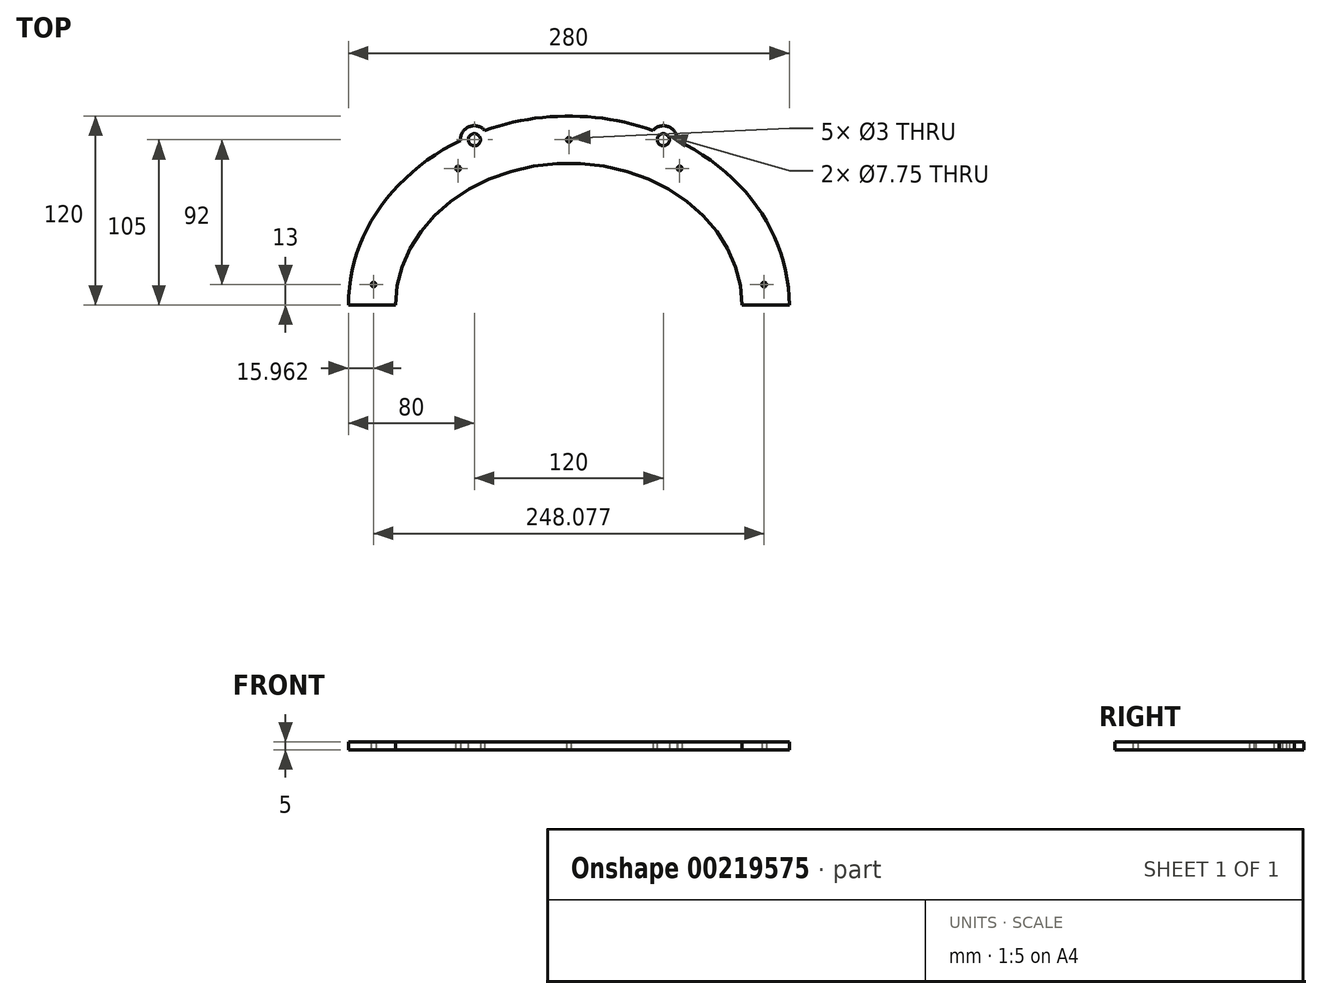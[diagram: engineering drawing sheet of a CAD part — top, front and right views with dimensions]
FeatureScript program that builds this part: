
annotation { "Feature Type Name" : "Feature", "Feature Type Description" : "" }
export const myFeature = defineFeature(function(context is Context, id is Id, definition is map)
    precondition{}
    {
        {
            var Q0;
            Q0=qCreatedBy(makeId("Top.planeOp"),FACE);
            var sketch = newSketch(context, id + "F0", { "sketchPlane" : qUnion([Q0])});
            skEllipse(sketch, "E0", {"center": v(0, 0) * mm, "majorRadius": 140 * mm, "minorRadius": 120 * mm, "majorAxis": v(1, 0)});
            skLineSegment(sketch, "E1", {"start": v(0, 0) * mm, "end": v(0, 120) * mm, "construction": true});
            skLineSegment(sketch, "E2", {"start": v(0, 0) * mm, "end": v(140, 0) * mm, "construction": true});
            skPoint(sketch, "E2.endSnap0", {"position": v(140, 0) * mm});
            skEllipse(sketch, "E3", {"center": v(0, 0) * mm, "majorRadius": 110 * mm, "minorRadius": 90 * mm, "majorAxis": v(1, 0)});
            skLineSegment(sketch, "E4", {"start": v(110, 0) * mm, "end": v(140, 0) * mm, "construction": true});
            skLineSegment(sketch, "E5", {"start": v(0, 90) * mm, "end": v(0, 120) * mm, "construction": true});
            skCircle(sketch, "E6", {"center": v(-60, 105) * mm, "radius": 3.88 * mm});
            skCircle(sketch, "E7", {"center": v(60, 105) * mm, "radius": 3.88 * mm});
            skLineSegment(sketch, "E8", {"start": v(-60, 105) * mm, "end": v(60, 105) * mm, "construction": true});
            skPoint(sketch, "E9", {"position": v(0, 105) * mm});
            skLineSegment(sketch, "E10", {"start": v(-110, 0) * mm, "end": v(-140, 0) * mm});
            skLineSegment(sketch, "E11", {"start": v(110, 0) * mm, "end": v(140, 0) * mm});
            skPoint(sketch, "E12", {"position": v(125, 0) * mm});
            skEllipse(sketch, "E13", {"center": v(0, 0) * mm, "majorRadius": 125 * mm, "minorRadius": 105 * mm, "majorAxis": v(1, 0), "construction": true});
            skLineSegment(sketch, "E14", {"start": v(0, 0) * mm, "end": v(70.33, 86.8) * mm, "construction": true});
            skLineSegment(sketch, "E15", {"start": v(-124.04, 13) * mm, "end": v(0, 0) * mm, "construction": true});
            skLineSegment(sketch, "E16", {"start": v(0, 0) * mm, "end": v(-70.33, 86.8) * mm, "construction": true});
            skLineSegment(sketch, "E17", {"start": v(0, 0) * mm, "end": v(124.04, 13) * mm, "construction": true});
            skCircle(sketch, "E18", {"center": v(-124.04, 13) * mm, "radius": 1.5 * mm});
            skCircle(sketch, "E19", {"center": v(-70.33, 86.8) * mm, "radius": 1.5 * mm});
            skCircle(sketch, "E20", {"center": v(70.33, 86.8) * mm, "radius": 1.5 * mm});
            skCircle(sketch, "E21", {"center": v(124.04, 13) * mm, "radius": 1.5 * mm});
            skCircle(sketch, "E22", {"center": v(0, 105) * mm, "radius": 1.5 * mm});
            skCircle(sketch, "E23", {"center": v(-60, 105) * mm, "radius": 8.88 * mm});
            skCircle(sketch, "E24", {"center": v(60, 105) * mm, "radius": 8.88 * mm});
            skSolve(sketch);
        }
        {
            var Q0;
            Q0=makeQuery(id+"F0.imprint","IMPRINT",FACE,{"disambiguationData":[TD([[makeQuery(id+"F0.imprint","IMPRINT",EDGE,{"derivedFrom":sQuery(id+"F0.wireOp",EDGE,"E6")}),-1.0]])]});
            var Q1;
            {var subQ8=sQuery(id+"F0.wireOp",EDGE,"E10");Q1=makeQuery(id+"F0.imprint","IMPRINT",FACE,{"disambiguationData":[TD([[makeQuery(id+"F0.imprint","IMPRINT",EDGE,{"derivedFrom":subQ8}),-1.0]])]});}
            var Q2;
            Q2=makeQuery(id+"F0.imprint","IMPRINT",FACE,{"disambiguationData":[TD([[makeQuery(id+"F0.imprint","IMPRINT",EDGE,{"derivedFrom":sQuery(id+"F0.wireOp",EDGE,"E7")}),-1.0]])]});
            var Q3;
            {var subQ0=sQuery(id+"F0.wireOp",EDGE,"E24");var subQ1=sQuery(id+"F0.wireOp",EDGE,"E3");var subQ2=makeQuery(id+"F0.imprint","INTERSECT",VERTEX,{"disambiguationData":[OD(0.0)],"derivedFrom":[subQ1,subQ0]});Q3=makeQuery(id+"F0.imprint","IMPRINT",FACE,{"disambiguationData":[TD([[makeQuery(id+"F0.imprint","IMPRINT",EDGE,{"disambiguationData":[TD([[subQ2,-1.0]])],"derivedFrom":subQ1}),-1.0]])]});}
            var Q4;
            {var subQ0=sQuery(id+"F0.wireOp",EDGE,"E23");var subQ1=sQuery(id+"F0.wireOp",EDGE,"E3");var subQ2=makeQuery(id+"F0.imprint","INTERSECT",VERTEX,{"disambiguationData":[OD(0.0)],"derivedFrom":[subQ1,subQ0]});Q4=makeQuery(id+"F0.imprint","IMPRINT",FACE,{"disambiguationData":[TD([[makeQuery(id+"F0.imprint","IMPRINT",EDGE,{"disambiguationData":[TD([[subQ2,1.0]])],"derivedFrom":subQ1}),-1.0]])]});}
            var Q5;
            {var subQ0=sQuery(id+"F0.wireOp",EDGE,"E23");var subQ1=sQuery(id+"F0.wireOp",EDGE,"E0");var subQ2=makeQuery(id+"F0.imprint","INTERSECT",VERTEX,{"disambiguationData":[OD(0.0)],"derivedFrom":[subQ1,subQ0]});Q5=makeQuery(id+"F0.imprint","IMPRINT",FACE,{"disambiguationData":[TD([[makeQuery(id+"F0.imprint","IMPRINT",EDGE,{"disambiguationData":[TD([[subQ2,-1.0]])],"derivedFrom":subQ1}),-1.0]])]});}
            var Q6;
            {var subQ0=sQuery(id+"F0.wireOp",EDGE,"E24");var subQ1=sQuery(id+"F0.wireOp",EDGE,"E0");var subQ2=makeQuery(id+"F0.imprint","INTERSECT",VERTEX,{"disambiguationData":[OD(0.0)],"derivedFrom":[subQ1,subQ0]});Q6=makeQuery(id+"F0.imprint","IMPRINT",FACE,{"disambiguationData":[TD([[makeQuery(id+"F0.imprint","IMPRINT",EDGE,{"disambiguationData":[TD([[subQ2,-1.0]])],"derivedFrom":subQ1}),-1.0]])]});}
            extrude(context, id + "F1", {"entities" : qUnion([Q0, Q1, Q2, Q3, Q4, Q5, Q6]), "depth" : 5 * mm});
        }
    });
